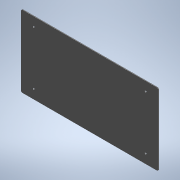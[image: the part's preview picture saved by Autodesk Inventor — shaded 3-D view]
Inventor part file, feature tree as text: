
AUTODESK INVENTOR PART (.ipt)
format: ipt  version: 2021.3 (Build 253353000, 353)  size: 114,688 bytes
history: native  units: mm
features: sketch x2, extrude x1, hole x1, fillet x1
ambient origin geometry x8: Origin, YZ Plane, XZ Plane, XY Plane, X Axis, Y Axis, Z Axis, Center Point
bodies: Volumenkörper1 (feature_tree)
feature tree (5):
  extrude  "Extrusion1"  Depth=1.5mm
  hole  "Bohrung1"  [1 undecoded]
  fillet  "Rundung1"  Radius=160.0mm
  sketch  "Skizze1"  dims[d0=306.0mm d1=1.5mm]
  sketch  "Skizze2"  dims[d2=160.0mm d3=0.0mm d4=306.0mm d5=160.0mm d6=153.0mm d7=80.0mm d8=250.0mm d9=120.0mm d10=4.5mm d11=6.0mm d12=4.0mm d13=2.0mm d14=90.0deg d15=11.8mm d16=20.594885mm d17=3.0mm]
note: 1 required parameter value undecoded (feature->parameter linkage not recoverable at this tier; creation-order binding heuristic only, values carry confidence <= 0.55)
